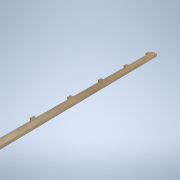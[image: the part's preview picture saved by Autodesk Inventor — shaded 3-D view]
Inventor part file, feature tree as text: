
AUTODESK INVENTOR PART (.ipt)
format: ipt  version: 2021 (Build 250183000, 183)  size: 137,216 bytes
history: native  units: mm
features: extrude x1, sketch x1
ambient origin geometry x8: Origin, YZ Plane, XZ Plane, XY Plane, X Axis, Y Axis, Z Axis, Center Point
bodies: Solid1 (feature_tree)
feature tree (2):
  extrude  "Extrusion1"  Depth=3.0mm
  sketch  "Sketch1"  dims[d4=3.0mm d5=0.0mm d10=3.0mm d16=60.0mm d18=38.0mm d19=10.0mm d21=10.0mm d11=0.5mm d12=0.872665mm d13=0.5mm d14=0.872665mm]
